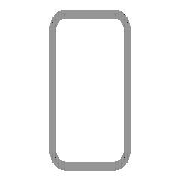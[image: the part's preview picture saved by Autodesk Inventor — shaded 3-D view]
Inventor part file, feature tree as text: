
AUTODESK INVENTOR PART (.ipt)
format: ipt  version: 2025.3 (Build 293356030, 356C)  size: 148,992 bytes
history: native  units: mm (DEFAULTED — no unit token found)
features: other x4, plane x3, split x2, sketch x1
ambient origin geometry x8: Origin, YZ Plane, XZ Plane, XY Plane, X Axis, Y Axis, Z Axis, Center Point
bodies: Solid1 (feature_tree), Body (feature_tree)
feature tree (10):
  parser-record x1  (decoder bookkeeping rows leaked as tree rows — omitted from the tree; the rows remain in map.json)
  other  "Driven Length"
  other  "Start Plane"
  other  "End Plane"
  plane  "Work Plane4"
  split  "Split1"
  plane  "Work Plane5"
  split  "Split2"
  sketch  "Sketch3"  dims[d3=2701.920698mm d4=0.0mm d7=4.0mm d9=20.0mm d11=40.0mm d12=2.0mm d13=126.334848mm d14=2828.255546mm d15=10.0mm d16=20.0mm d17=90.0deg d18=2701.920698mm]
  plane  "Work Plane3"
